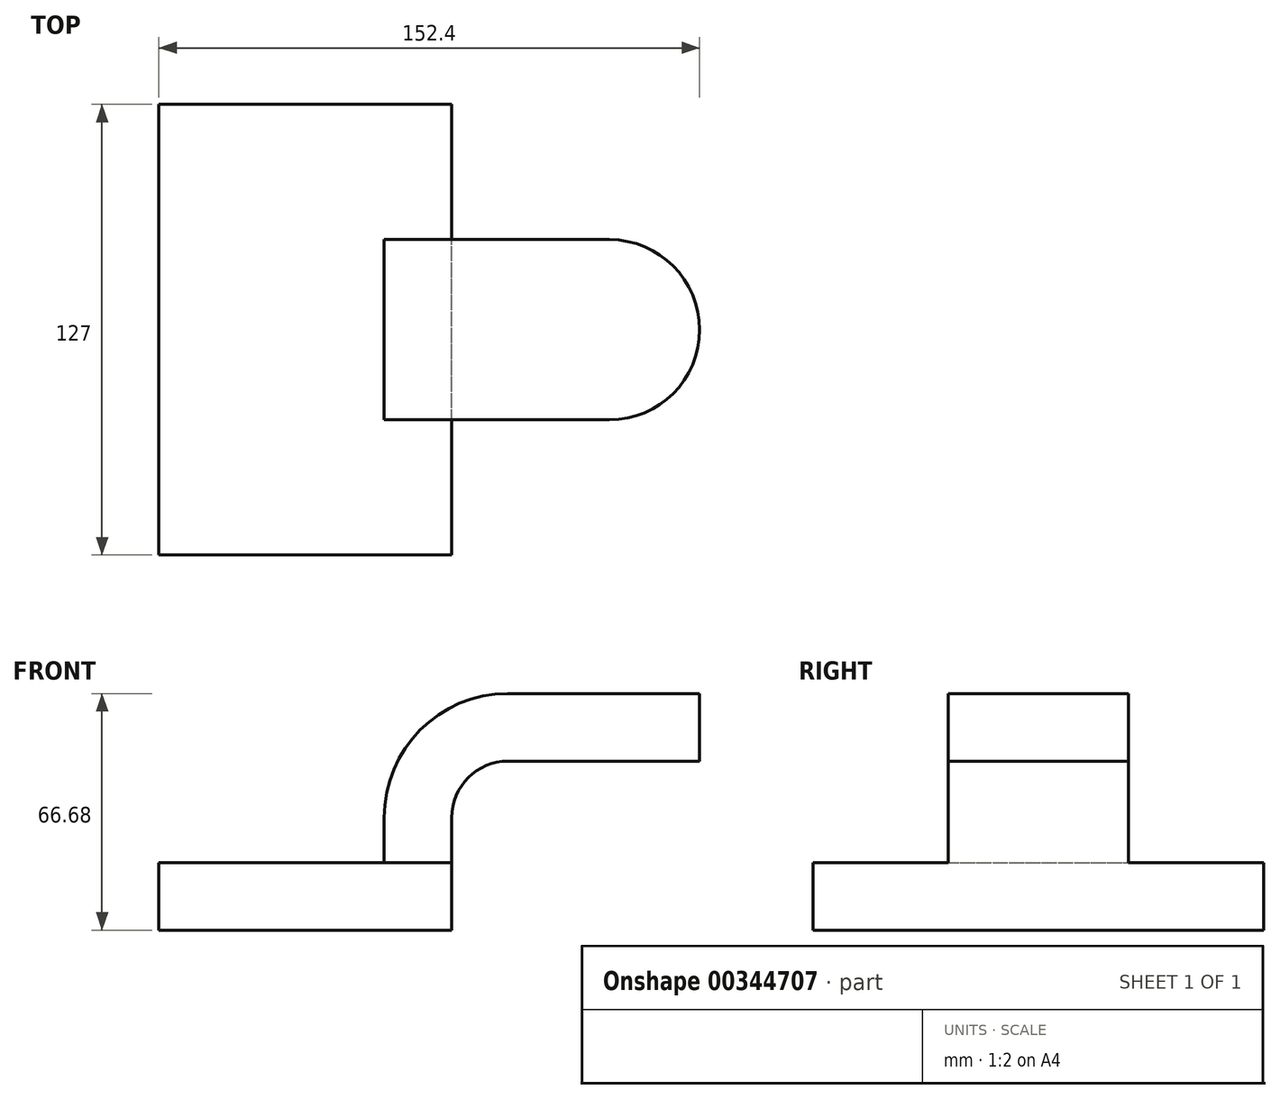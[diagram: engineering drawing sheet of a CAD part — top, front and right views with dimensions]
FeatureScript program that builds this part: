
annotation { "Feature Type Name" : "Feature", "Feature Type Description" : "" }
export const myFeature = defineFeature(function(context is Context, id is Id, definition is map)
    precondition{}
    {
        {
            var Q0;
            Q0=qCreatedBy(makeId("Front.planeOp"),FACE);
            var sketch = newSketch(context, id + "F0", { "sketchPlane" : qUnion([Q0])});
            skLineSegment(sketch, "E0.bottom", {"start": v(-41.28, 9.52) * mm, "end": v(41.27, 9.53) * mm});
            skLineSegment(sketch, "E0.top", {"start": v(-41.28, -9.53) * mm, "end": v(41.28, -9.53) * mm});
            skLineSegment(sketch, "E0.left", {"start": v(-41.28, 9.52) * mm, "end": v(-41.28, -9.53) * mm});
            skLineSegment(sketch, "E0.right", {"start": v(41.27, 9.53) * mm, "end": v(41.28, -9.52) * mm});
            skPoint(sketch, "E0.middle", {"position": v(0, 0) * mm});
            skLineSegment(sketch, "E1.bottom", {"start": v(60.33, 38.1) * mm, "end": v(111.12, 38.1) * mm});
            skLineSegment(sketch, "E1.top", {"start": v(60.33, 66.68) * mm, "end": v(111.12, 66.68) * mm});
            skLineSegment(sketch, "E1.left", {"start": v(60.33, 38.1) * mm, "end": v(60.33, 66.67) * mm});
            skLineSegment(sketch, "E1.right", {"start": v(111.12, 38.1) * mm, "end": v(111.12, 66.68) * mm});
            skPoint(sketch, "E1.middle", {"position": v(85.72, 52.39) * mm});
            skLineSegment(sketch, "E2", {"start": v(41.27, 9.53) * mm, "end": v(41.27, 22.23) * mm});
            skArc(sketch, "E3", {"start": v(41.27, 22.23) * mm, "mid": v(45.92, 33.45) * mm, "end": v(57.15, 38.1) * mm});
            skLineSegment(sketch, "E4", {"start": v(57.15, 38.1) * mm, "end": v(85.72, 38.1) * mm});
            skLineSegment(sketch, "E5.0", {"start": v(57.15, 57.15) * mm, "end": v(85.72, 57.15) * mm});
            skArc(sketch, "E5.1", {"start": v(22.22, 22.22) * mm, "mid": v(32.45, 46.92) * mm, "end": v(57.15, 57.15) * mm});
            skLineSegment(sketch, "E5.2", {"start": v(22.22, 9.53) * mm, "end": v(22.22, 22.22) * mm});
            skLineSegment(sketch, "E6", {"start": v(85.72, 57.15) * mm, "end": v(85.72, 66.68) * mm});
            skLineSegment(sketch, "E7", {"start": v(85.72, 66.68) * mm, "end": v(85.72, 38.1) * mm});
            skFitSpline(sketch, "E8", {"points": [v(-41.28, 9.53) * mm, v(57.15, 57.15) * mm], "startDerivative": vector(49.04, 121.03) * mm, "endDerivative": vector(128.08, 0.23) * mm});
            skSolve(sketch);
        }
        {
            var Q0;
            Q0=makeQuery(id+"F0.imprint","IMPRINT",FACE,{"disambiguationData":[TD([[makeQuery(id+"F0.imprint","IMPRINT",EDGE,{"derivedFrom":sQuery(id+"F0.wireOp",EDGE,"E0.top")}),1.0]])]});
            extrude(context, id + "F1", {"entities" : qUnion([Q0]), "endBound" : BoundingType.SYMMETRIC, "depth" : 127 * mm});
        }
        {
            var Q0;
            {var subQ1=sQuery(id+"F0.wireOp",EDGE,"E2");Q0=makeQuery(id+"F0.imprint","IMPRINT",FACE,{"disambiguationData":[TD([[makeQuery(id+"F0.imprint","IMPRINT",EDGE,{"derivedFrom":subQ1}),1.0]])]});}
            var Q1;
            {var subQ0=sQuery(id+"F0.wireOp",EDGE,"E4");var subQ1=sQuery(id+"F0.wireOp",EDGE,"E1.left");var subQ2=makeQuery(id+"F0.imprint","INTERSECT",VERTEX,{"derivedFrom":[subQ1,subQ0]});Q1=makeQuery(id+"F0.imprint","IMPRINT",FACE,{"disambiguationData":[TD([[makeQuery(id+"F0.imprint","IMPRINT",EDGE,{"disambiguationData":[TD([[subQ2,-1.0]])],"derivedFrom":subQ1}),-1.0]])]});}
            extrude(context, id + "F2", {"entities" : qUnion([Q0, Q1]), "operationType" : NewBodyOperationType.ADD, "endBound" : BoundingType.SYMMETRIC, "depth" : 50.8 * mm});
        }
        {
            var Q0;
            {var subQ4=sQuery(id+"F0.wireOp",EDGE,"E5.1");Q0=makeQuery(id+"F0.imprint","IMPRINT",FACE,{"disambiguationData":[TD([[makeQuery(id+"F0.imprint","IMPRINT",EDGE,{"derivedFrom":subQ4}),1.0]])]});}
            extrude(context, id + "F3", {"entities" : qUnion([Q0]), "operationType" : NewBodyOperationType.ADD, "endBound" : BoundingType.SYMMETRIC, "depth" : 16.5 * mm});
        }
        {
            var Q0;
            {var subQ5=sQuery(id+"F0.wireOp",EDGE,"E1.bottom");Q0=makeQuery(id+"F0.imprint","IMPRINT",FACE,{"disambiguationData":[TD([[makeQuery(id+"F0.imprint","IMPRINT",EDGE,{"derivedFrom":subQ5}),1.0]])]});}
            var Q1;
            Q1=sQuery(id+"F0.wireOp",EDGE,"E7");
            revolve(context, id + "F4", {"operationType" : NewBodyOperationType.ADD, "entities" : qUnion([Q0]), "axis" : qUnion([Q1]), "revolveType" : RevolveType.FULL});
        }
    });
